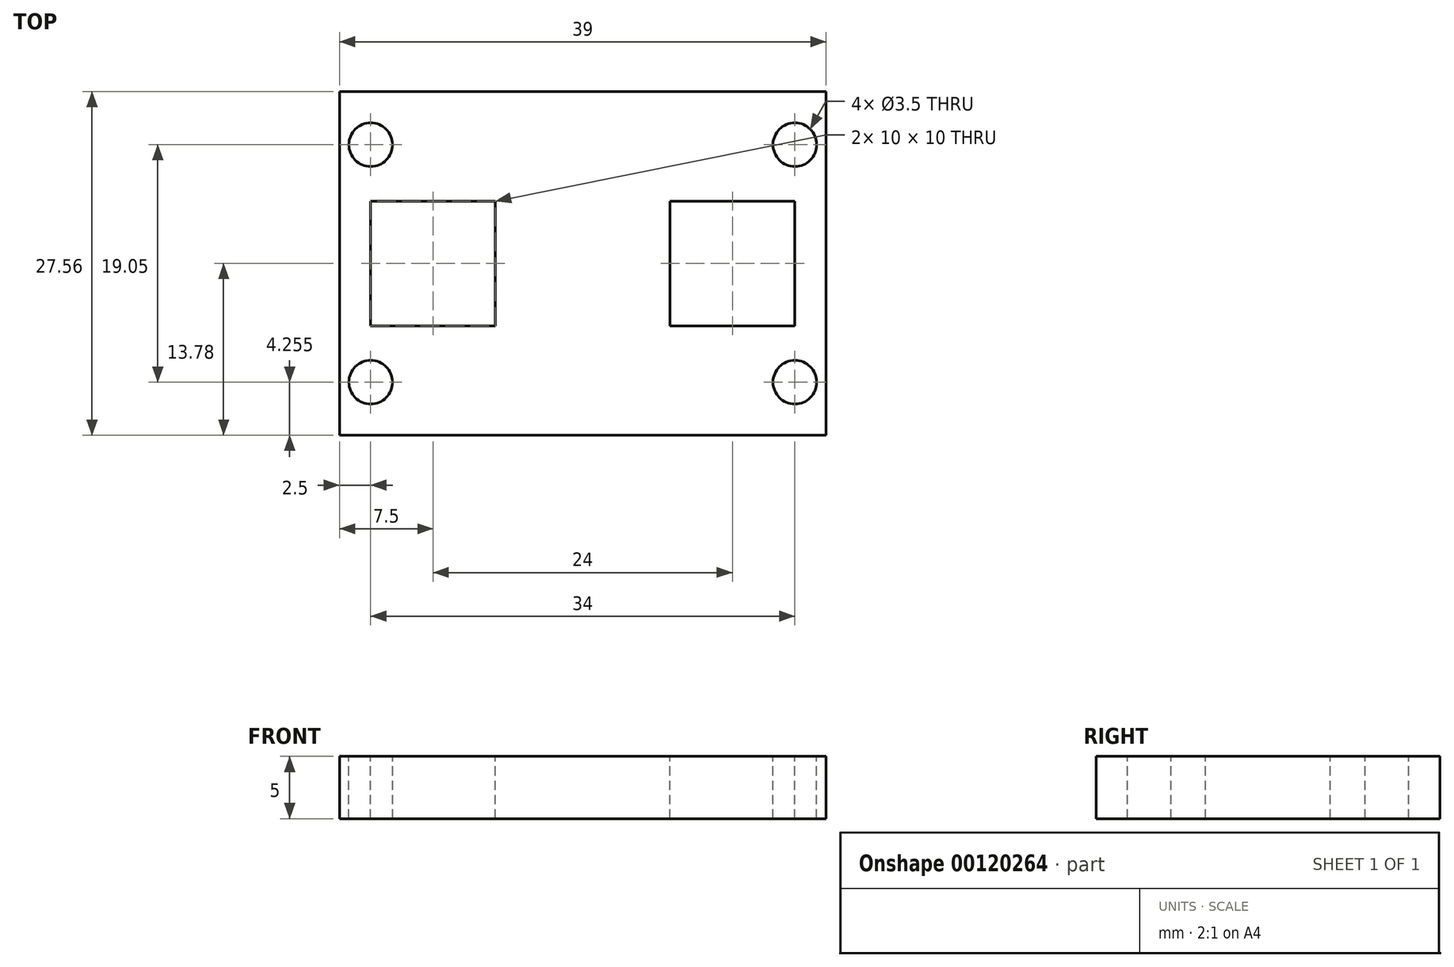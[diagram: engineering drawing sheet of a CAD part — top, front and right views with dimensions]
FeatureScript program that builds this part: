
annotation { "Feature Type Name" : "Feature", "Feature Type Description" : "" }
export const myFeature = defineFeature(function(context is Context, id is Id, definition is map)
    precondition{}
    {
        {
            var Q0;
            Q0=qCreatedBy(makeId("Top.planeOp"),FACE);
            var sketch = newSketch(context, id + "F0", { "sketchPlane" : qUnion([Q0])});
            skLineSegment(sketch, "E0.bottom", {"start": v(19.5, 13.78) * mm, "end": v(-19.5, 13.78) * mm});
            skLineSegment(sketch, "E0.top", {"start": v(19.5, -13.78) * mm, "end": v(-19.5, -13.78) * mm});
            skLineSegment(sketch, "E0.left", {"start": v(19.5, 13.78) * mm, "end": v(19.5, -13.78) * mm});
            skLineSegment(sketch, "E0.right", {"start": v(-19.5, 13.78) * mm, "end": v(-19.5, -13.78) * mm});
            skPoint(sketch, "E0.middle", {"position": v(0, 0) * mm});
            skSolve(sketch);
        }
        {
            var Q0;
            Q0 = qSketchRegion(id + "F0", true);
            extrude(context, id + "F1", {"entities" : qUnion([Q0]), "depth" : 5 * mm});
        }
        {
            var Q0;
            Q0=makeQuery(id+"F1.opExtrude","CAP_FACE",FACE,{"disambiguationData":[OSD([sQuery(id+"F0.wireOp",EDGE,"E0.bottom"),sQuery(id+"F0.wireOp",EDGE,"E0.top"),sQuery(id+"F0.wireOp",EDGE,"E0.left"),sQuery(id+"F0.wireOp",EDGE,"E0.right")])],"isStart":false});
            var sketch = newSketch(context, id + "F2", { "sketchPlane" : qUnion([Q0])});
            skCircle(sketch, "E1", {"center": v(-17, 9.53) * mm, "radius": 1.75 * mm});
            skCircle(sketch, "E2", {"center": v(-17, -9.53) * mm, "radius": 1.75 * mm});
            skCircle(sketch, "E3", {"center": v(17, -9.53) * mm, "radius": 1.75 * mm});
            skCircle(sketch, "E4", {"center": v(17, 9.53) * mm, "radius": 1.75 * mm});
            skSolve(sketch);
        }
        {
            var Q0;
            Q0 = qSketchRegion(id + "F2", true);
            extrude(context, id + "F3", {"entities" : qUnion([Q0]), "operationType" : NewBodyOperationType.REMOVE, "oppositeDirection" : true, "depth" : 25 * mm});
        }
        {
            var Q0;
            Q0=makeQuery(id+"F1.opExtrude","CAP_FACE",FACE,{"disambiguationData":[OSD([sQuery(id+"F0.wireOp",EDGE,"E0.bottom"),sQuery(id+"F0.wireOp",EDGE,"E0.top"),sQuery(id+"F0.wireOp",EDGE,"E0.left"),sQuery(id+"F0.wireOp",EDGE,"E0.right")])],"isStart":false});
            var sketch = newSketch(context, id + "F4", { "sketchPlane" : qUnion([Q0])});
            skLineSegment(sketch, "E5.bottom", {"start": v(-17, -5) * mm, "end": v(-7, -5) * mm});
            skLineSegment(sketch, "E5.top", {"start": v(-17, 5) * mm, "end": v(-7, 5) * mm});
            skLineSegment(sketch, "E5.left", {"start": v(-17, -5) * mm, "end": v(-17, 5) * mm});
            skLineSegment(sketch, "E5.right", {"start": v(-7, -5) * mm, "end": v(-7, 5) * mm});
            skLineSegment(sketch, "E6.bottom", {"start": v(7, -5) * mm, "end": v(17, -5) * mm});
            skLineSegment(sketch, "E6.top", {"start": v(7, 5) * mm, "end": v(17, 5) * mm});
            skLineSegment(sketch, "E6.left", {"start": v(7, -5) * mm, "end": v(7, 5) * mm});
            skLineSegment(sketch, "E6.right", {"start": v(17, -5) * mm, "end": v(17, 5) * mm});
            skSolve(sketch);
        }
        {
            var Q0;
            Q0 = qSketchRegion(id + "F4", true);
            extrude(context, id + "F5", {"entities" : qUnion([Q0]), "operationType" : NewBodyOperationType.REMOVE, "oppositeDirection" : true, "depth" : 25 * mm});
        }
    });
